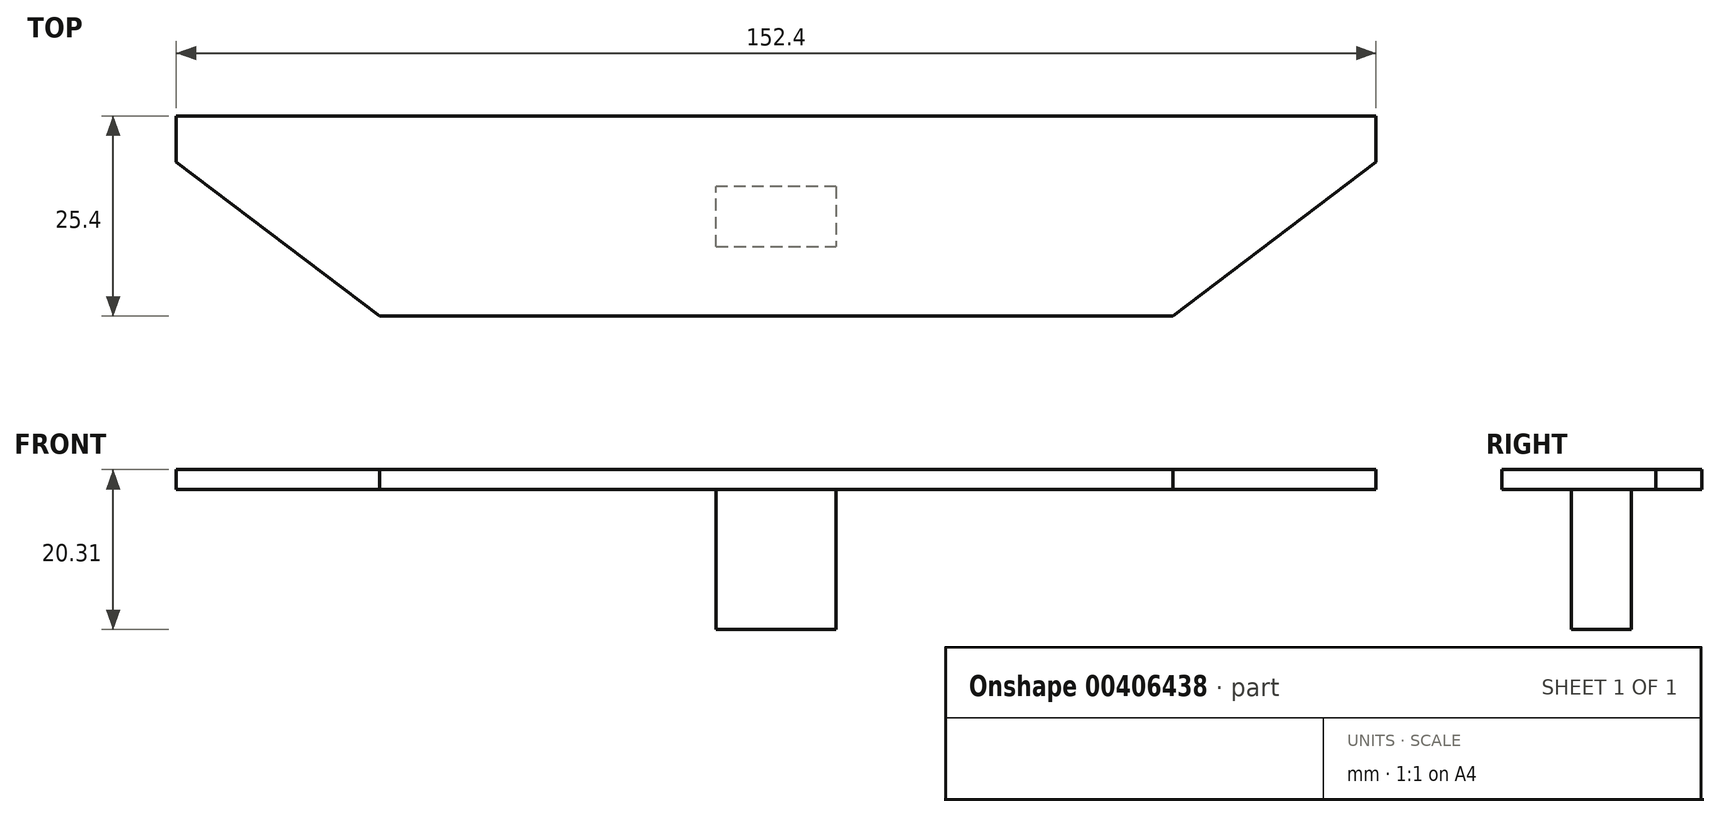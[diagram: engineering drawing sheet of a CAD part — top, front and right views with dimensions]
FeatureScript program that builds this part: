
annotation { "Feature Type Name" : "Feature", "Feature Type Description" : "" }
export const myFeature = defineFeature(function(context is Context, id is Id, definition is map)
    precondition{}
    {
        {
            var Q0;
            Q0=qCreatedBy(makeId("Right.planeOp"),FACE);
            var sketch = newSketch(context, id + "F0", { "sketchPlane" : qUnion([Q0])});
            skLineSegment(sketch, "E0.bottom", {"start": v(14.93, 2.6) * mm, "end": v(22.55, 2.6) * mm});
            skLineSegment(sketch, "E0.top", {"start": v(14.93, -15.17) * mm, "end": v(22.55, -15.17) * mm});
            skLineSegment(sketch, "E0.left", {"start": v(14.93, 2.6) * mm, "end": v(14.93, -15.17) * mm});
            skLineSegment(sketch, "E0.right", {"start": v(22.55, 2.6) * mm, "end": v(22.55, -15.17) * mm});
            skSolve(sketch);
        }
        {
            var Q0;
            Q0=makeQuery(id+"F0.imprint","IMPRINT",FACE,{"disambiguationData":[TD([[makeQuery(id+"F0.imprint","IMPRINT",EDGE,{"derivedFrom":sQuery(id+"F0.wireOp",EDGE,"E0.bottom")}),-1.0]])]});
            extrude(context, id + "F1", {"entities" : qUnion([Q0]), "depth" : 7.62 * mm});
        }
        {
            var Q0;
            Q0=qCreatedBy(makeId("Right.planeOp"),FACE);
            var sketch = newSketch(context, id + "F2", { "sketchPlane" : qUnion([Q0])});
            skLineSegment(sketch, "E1.bottom", {"start": v(6.12, 5.14) * mm, "end": v(31.52, 5.14) * mm});
            skLineSegment(sketch, "E1.top", {"start": v(6.12, 2.6) * mm, "end": v(31.52, 2.6) * mm});
            skLineSegment(sketch, "E1.left", {"start": v(6.12, 5.14) * mm, "end": v(6.12, 2.6) * mm});
            skLineSegment(sketch, "E1.right", {"start": v(31.52, 5.14) * mm, "end": v(31.52, 2.6) * mm});
            skSolve(sketch);
        }
        {
            var Q0;
            Q0=makeQuery(id+"F2.imprint","IMPRINT",FACE,{"disambiguationData":[TD([[makeQuery(id+"F2.imprint","IMPRINT",EDGE,{"derivedFrom":sQuery(id+"F2.wireOp",EDGE,"E1.bottom")}),-1.0]])]});
            extrude(context, id + "F3", {"entities" : qUnion([Q0]), "operationType" : NewBodyOperationType.ADD, "depth" : 76.2 * mm});
        }
        {
            var Q0;
            Q0=makeQuery(id+"F3.opExtrude","SWEPT_FACE",FACE,{"disambiguationData":[OSD([sQuery(id+"F2.wireOp",EDGE,"E1.bottom")])]});
            var sketch = newSketch(context, id + "F4", { "sketchPlane" : qUnion([Q0])});
            skLineSegment(sketch, "E2", {"start": v(76.2, 25.7) * mm, "end": v(50.4, 6.12) * mm});
            skSolve(sketch);
        }
        {
            var Q0;
            {var subQ0=sQuery(id+"F4.wireOp",EDGE,"E2");Q0=makeQuery(id+"F4.imprint","IMPRINT",FACE,{"disambiguationData":[TD([[makeQuery(id+"F4.imprint","IMPRINT",EDGE,{"derivedFrom":subQ0}),1.0]])]});}
            extrude(context, id + "F5", {"entities" : qUnion([Q0]), "operationType" : NewBodyOperationType.REMOVE, "oppositeDirection" : true, "depth" : 50.8 * mm});
        }
        {
            var Q0;
            Q0=makeQuery(id+"F1.opExtrude","SWEPT_BODY",BODY,{"disambiguationData":[OSD([sQuery(id+"F0.wireOp",EDGE,"E0.bottom"),sQuery(id+"F0.wireOp",EDGE,"E0.top"),sQuery(id+"F0.wireOp",EDGE,"E0.left"),sQuery(id+"F0.wireOp",EDGE,"E0.right")])]});
            var Q1;
            Q1=qCreatedBy(makeId("Right.planeOp"),FACE);
            mirror(context, id + "F6", {"operationType" : NewBodyOperationType.ADD, "entities" : qUnion([Q0]), "mirrorPlane" : qUnion([Q1])});
        }
    });
